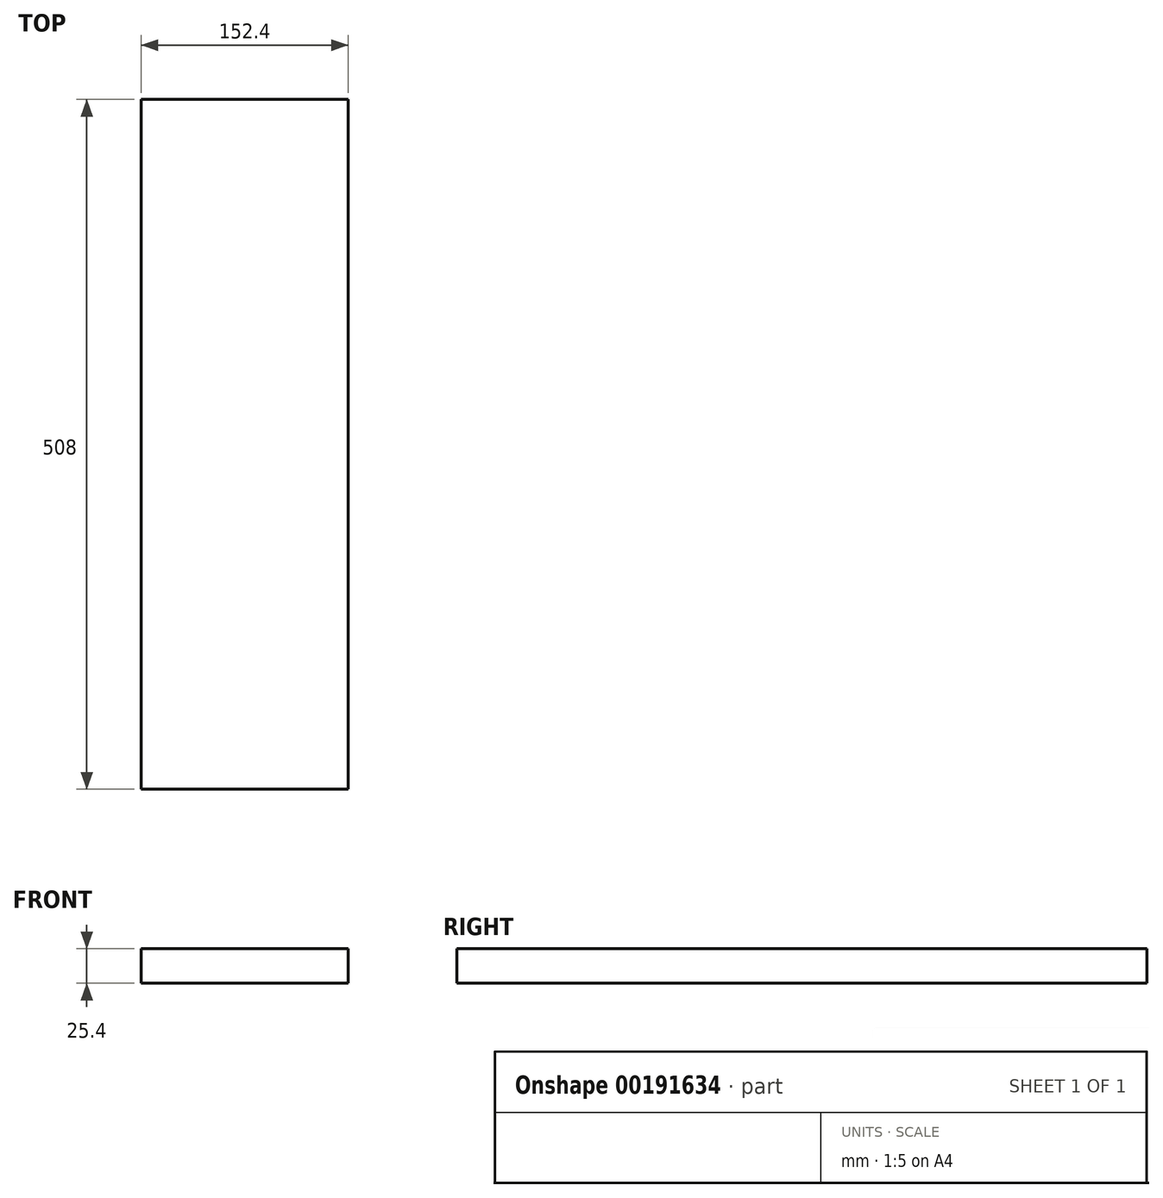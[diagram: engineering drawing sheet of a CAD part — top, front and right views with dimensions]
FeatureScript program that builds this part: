
annotation { "Feature Type Name" : "Feature", "Feature Type Description" : "" }
export const myFeature = defineFeature(function(context is Context, id is Id, definition is map)
    precondition{}
    {
        {
            var Q0;
            Q0=qCreatedBy(makeId("Right.planeOp"),FACE);
            var sketch = newSketch(context, id + "F0", { "sketchPlane" : qUnion([Q0])});
            skLineSegment(sketch, "E0.bottom", {"start": v(0, 0) * mm, "end": v(-508, 0) * mm});
            skLineSegment(sketch, "E0.top", {"start": v(0, 25.4) * mm, "end": v(-508, 25.4) * mm});
            skLineSegment(sketch, "E0.left", {"start": v(0, 0) * mm, "end": v(0, 25.4) * mm});
            skLineSegment(sketch, "E0.right", {"start": v(-508, 0) * mm, "end": v(-508, 25.4) * mm});
            skSolve(sketch);
        }
        {
            var Q0;
            Q0=makeQuery(id+"F0.imprint","IMPRINT",FACE,{"disambiguationData":[TD([[makeQuery(id+"F0.imprint","IMPRINT",EDGE,{"derivedFrom":sQuery(id+"F0.wireOp",EDGE,"E0.bottom")}),-1.0]])]});
            extrude(context, id + "F1", {"entities" : qUnion([Q0]), "depth" : 152.4 * mm});
        }
    });
